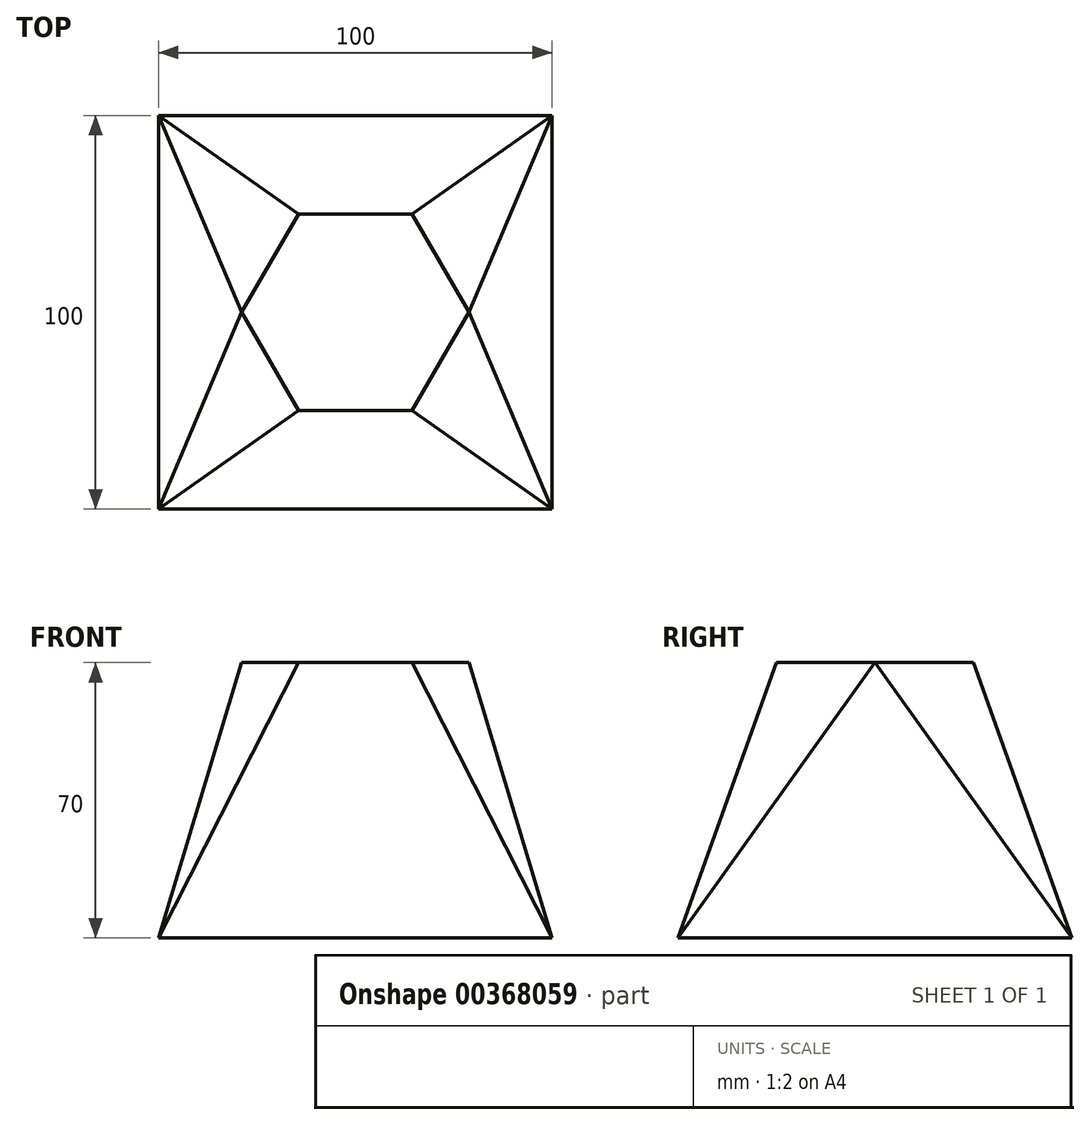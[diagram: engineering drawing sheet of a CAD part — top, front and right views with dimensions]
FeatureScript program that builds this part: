
annotation { "Feature Type Name" : "Feature", "Feature Type Description" : "" }
export const myFeature = defineFeature(function(context is Context, id is Id, definition is map)
    precondition{}
    {
        {
            var Q0;
            Q0=qCreatedBy(makeId("Top.planeOp"),FACE);
            cPlane(context, id + "F0", {"entities" : qUnion([Q0]), "cplaneType" : CPlaneType.OFFSET, "offset" : 70 * mm, "width" : 150 * mm, "height" : 150 * mm});
        }
        {
            var Q0;
            Q0=qCreatedBy(id+"F0.planeOp",FACE);
            var sketch = newSketch(context, id + "F1", { "sketchPlane" : qUnion([Q0])});
            skCircle(sketch, "E0.cCircle", {"center": v(0, 0) * mm, "radius": 25 * mm, "construction": true});
            skLineSegment(sketch, "E0.0", {"start": v(-14.43, 25) * mm, "end": v(14.43, 25) * mm});
            skLineSegment(sketch, "E0.1", {"start": v(14.43, 25) * mm, "end": v(28.87, 0) * mm});
            skLineSegment(sketch, "E0.2", {"start": v(28.87, 0) * mm, "end": v(14.43, -25) * mm});
            skLineSegment(sketch, "E0.3", {"start": v(14.43, -25) * mm, "end": v(-14.43, -25) * mm});
            skLineSegment(sketch, "E0.4", {"start": v(-14.43, -25) * mm, "end": v(-28.87, 0) * mm});
            skLineSegment(sketch, "E0.5", {"start": v(-28.87, 0) * mm, "end": v(-14.43, 25) * mm});
            skPoint(sketch, "E0.0.midPoint", {"position": v(0, 25) * mm});
            skLineSegment(sketch, "E1", {"start": v(14.43, 25) * mm, "end": v(14.43, -25) * mm});
            skLineSegment(sketch, "E2", {"start": v(-14.43, 25) * mm, "end": v(-14.43, -25) * mm});
            skSolve(sketch);
        }
        {
            var Q0;
            Q0=qCreatedBy(makeId("Top.planeOp"),FACE);
            var sketch = newSketch(context, id + "F2", { "sketchPlane" : qUnion([Q0])});
            skLineSegment(sketch, "E3.bottom", {"start": v(-50, 50) * mm, "end": v(50, 50) * mm});
            skLineSegment(sketch, "E3.top", {"start": v(-50, -50) * mm, "end": v(50, -50) * mm});
            skLineSegment(sketch, "E3.left", {"start": v(-50, 50) * mm, "end": v(-50, -50) * mm});
            skLineSegment(sketch, "E3.right", {"start": v(50, 50) * mm, "end": v(50, -50) * mm});
            skPoint(sketch, "E3.middle", {"position": v(0, 0) * mm});
            skSolve(sketch);
        }
        {
            var Q0;
            Q0=makeQuery(id+"F1.imprint","IMPRINT",FACE,{"disambiguationData":[TD([[makeQuery(id+"F1.imprint","IMPRINT",EDGE,{"derivedFrom":sQuery(id+"F1.wireOp",EDGE,"E0.0")}),-1.0]])]});
            var Q1;
            Q1=makeQuery(id+"F2.imprint","IMPRINT",FACE,{"disambiguationData":[TD([[makeQuery(id+"F2.imprint","IMPRINT",EDGE,{"derivedFrom":sQuery(id+"F2.wireOp",EDGE,"E3.bottom")}),-1.0]])]});
            loft(context, id + "F3", {"sheetProfilesArray" : [{ "sheetProfileEntities" : qUnion([Q0]) }, { "sheetProfileEntities" : qUnion([Q1]) }]});
        }
        {
            var Q1;
            Q1=makeQuery(id+"F1.imprint","IMPRINT",FACE,{"disambiguationData":[TD([[makeQuery(id+"F1.imprint","IMPRINT",EDGE,{"derivedFrom":sQuery(id+"F1.wireOp",EDGE,"E0.1")}),-1.0]])]});
            var Q2;
            Q2=makeQuery(id+"F3.opLoft","MID_CAP_VERTEX",VERTEX,{"disambiguationData":[OSD([sQuery(id+"F2.wireOp",EDGE,"E3.top"),sQuery(id+"F2.wireOp",EDGE,"E3.right")])],"capPos":1.0});
            loft(context, id + "F4", {"operationType" : NewBodyOperationType.ADD, "sheetProfilesArray" : [{ "sheetProfileEntities" : qUnion([Q1]) }, { "sheetProfileEntities" : qUnion([Q2]) }]});
        }
        {
            var Q1;
            Q1=makeQuery(id+"F1.imprint","IMPRINT",FACE,{"disambiguationData":[TD([[makeQuery(id+"F1.imprint","IMPRINT",EDGE,{"derivedFrom":sQuery(id+"F1.wireOp",EDGE,"E0.1")}),-1.0]])]});
            var Q2;
            Q2=makeQuery(id+"F3.opLoft","MID_CAP_VERTEX",VERTEX,{"disambiguationData":[OSD([sQuery(id+"F2.wireOp",EDGE,"E3.bottom"),sQuery(id+"F2.wireOp",EDGE,"E3.right")])],"capPos":1.0});
            loft(context, id + "F5", {"operationType" : NewBodyOperationType.ADD, "sheetProfilesArray" : [{ "sheetProfileEntities" : qUnion([Q1]) }, { "sheetProfileEntities" : qUnion([Q2]) }]});
        }
        {
            var Q1;
            Q1=makeQuery(id+"F4.opLoft","SWEPT_FACE",FACE,{"disambiguationData":[OSD([sQuery(id+"F1.wireOp",EDGE,"E0.0"),sQuery(id+"F1.wireOp",EDGE,"E0.1"),sQuery(id+"F1.wireOp",EDGE,"E0.2"),sQuery(id+"F1.wireOp",EDGE,"E1")])]});
            var Q2;
            Q2=makeQuery(id+"F5.opLoft","SWEPT_FACE",FACE,{"disambiguationData":[OSD([sQuery(id+"F1.wireOp",EDGE,"E0.1"),sQuery(id+"F1.wireOp",EDGE,"E0.2"),sQuery(id+"F1.wireOp",EDGE,"E0.3"),sQuery(id+"F1.wireOp",EDGE,"E1")])]});
            var Q3;
            {var subQ0=sQuery(id+"F2.wireOp",EDGE,"E3.right");var subQ1=sQuery(id+"F2.wireOp",EDGE,"E3.top");Q3=makeQuery(id+"F4.boolean.opBoolean","MERGE",VERTEX,{"derivedFrom":[makeQuery(id+"F3.opLoft","MID_CAP_VERTEX",VERTEX,{"disambiguationData":[OSD([subQ1,subQ0])],"capPos":1.0}),makeQuery(id+"F4.opLoft","SWEPT_VERTEX",VERTEX,{"disambiguationData":[OSD([sQuery(id+"F1.wireOp",EDGE,"E0.1"),sQuery(id+"F1.wireOp",EDGE,"E0.2"),subQ1,subQ0])]})]});}
            var Q4;
            {var subQ0=sQuery(id+"F2.wireOp",EDGE,"E3.right");var subQ1=sQuery(id+"F2.wireOp",EDGE,"E3.bottom");Q4=makeQuery(id+"F5.boolean.opBoolean","MERGE",VERTEX,{"derivedFrom":[makeQuery(id+"F3.opLoft","MID_CAP_VERTEX",VERTEX,{"disambiguationData":[OSD([subQ1,subQ0])],"capPos":1.0}),makeQuery(id+"F5.opLoft","SWEPT_VERTEX",VERTEX,{"disambiguationData":[OSD([sQuery(id+"F1.wireOp",EDGE,"E0.1"),sQuery(id+"F1.wireOp",EDGE,"E0.2"),subQ1,subQ0])]})]});}
            loft(context, id + "F6", {"operationType" : NewBodyOperationType.ADD, "sheetProfilesArray" : [{ "sheetProfileEntities" : qUnion([Q1]) }, { "sheetProfileEntities" : qUnion([Q2]) }], "matchConnections" : true, "connections" : [{ "connectionEntities" : qUnion([Q3, Q4]), "connectionEdgeQueries" : qUnion([]), "connectionEdgeParameters" : [] }]});
        }
        {
            var Q1;
            Q1=makeQuery(id+"F1.imprint","IMPRINT",FACE,{"disambiguationData":[TD([[makeQuery(id+"F1.imprint","IMPRINT",EDGE,{"derivedFrom":sQuery(id+"F1.wireOp",EDGE,"E0.4")}),-1.0]])]});
            var Q2;
            Q2=makeQuery(id+"F3.opLoft","MID_CAP_VERTEX",VERTEX,{"disambiguationData":[OSD([sQuery(id+"F2.wireOp",EDGE,"E3.top"),sQuery(id+"F2.wireOp",EDGE,"E3.left")])],"capPos":1.0});
            loft(context, id + "F7", {"operationType" : NewBodyOperationType.ADD, "sheetProfilesArray" : [{ "sheetProfileEntities" : qUnion([Q1]) }, { "sheetProfileEntities" : qUnion([Q2]) }]});
        }
        {
            var Q1;
            Q1=makeQuery(id+"F1.imprint","IMPRINT",FACE,{"disambiguationData":[TD([[makeQuery(id+"F1.imprint","IMPRINT",EDGE,{"derivedFrom":sQuery(id+"F1.wireOp",EDGE,"E0.4")}),-1.0]])]});
            var Q2;
            Q2=makeQuery(id+"F3.opLoft","MID_CAP_VERTEX",VERTEX,{"disambiguationData":[OSD([sQuery(id+"F2.wireOp",EDGE,"E3.bottom"),sQuery(id+"F2.wireOp",EDGE,"E3.left")])],"capPos":1.0});
            loft(context, id + "F8", {"operationType" : NewBodyOperationType.ADD, "sheetProfilesArray" : [{ "sheetProfileEntities" : qUnion([Q1]) }, { "sheetProfileEntities" : qUnion([Q2]) }]});
        }
        {
            var Q1;
            Q1=makeQuery(id+"F7.opLoft","SWEPT_FACE",FACE,{"disambiguationData":[OSD([sQuery(id+"F1.wireOp",EDGE,"E0.0"),sQuery(id+"F1.wireOp",EDGE,"E0.4"),sQuery(id+"F1.wireOp",EDGE,"E0.5"),sQuery(id+"F1.wireOp",EDGE,"E2")])]});
            var Q2;
            Q2=makeQuery(id+"F8.opLoft","SWEPT_FACE",FACE,{"disambiguationData":[OSD([sQuery(id+"F1.wireOp",EDGE,"E0.3"),sQuery(id+"F1.wireOp",EDGE,"E0.4"),sQuery(id+"F1.wireOp",EDGE,"E0.5"),sQuery(id+"F1.wireOp",EDGE,"E2")])]});
            var Q3;
            {var subQ0=sQuery(id+"F2.wireOp",EDGE,"E3.left");var subQ1=sQuery(id+"F2.wireOp",EDGE,"E3.bottom");Q3=makeQuery(id+"F8.boolean.opBoolean","MERGE",VERTEX,{"derivedFrom":[makeQuery(id+"F3.opLoft","MID_CAP_VERTEX",VERTEX,{"disambiguationData":[OSD([subQ1,subQ0])],"capPos":1.0}),makeQuery(id+"F8.opLoft","SWEPT_VERTEX",VERTEX,{"disambiguationData":[OSD([sQuery(id+"F1.wireOp",EDGE,"E0.3"),sQuery(id+"F1.wireOp",EDGE,"E0.4"),sQuery(id+"F1.wireOp",EDGE,"E2"),subQ1,subQ0])]})]});}
            var Q4;
            {var subQ0=sQuery(id+"F2.wireOp",EDGE,"E3.left");var subQ1=sQuery(id+"F2.wireOp",EDGE,"E3.top");Q4=makeQuery(id+"F7.boolean.opBoolean","MERGE",VERTEX,{"derivedFrom":[makeQuery(id+"F3.opLoft","MID_CAP_VERTEX",VERTEX,{"disambiguationData":[OSD([subQ1,subQ0])],"capPos":1.0}),makeQuery(id+"F7.opLoft","SWEPT_VERTEX",VERTEX,{"disambiguationData":[OSD([sQuery(id+"F1.wireOp",EDGE,"E0.3"),sQuery(id+"F1.wireOp",EDGE,"E0.4"),sQuery(id+"F1.wireOp",EDGE,"E2"),subQ1,subQ0])]})]});}
            loft(context, id + "F9", {"operationType" : NewBodyOperationType.ADD, "sheetProfilesArray" : [{ "sheetProfileEntities" : qUnion([Q1]) }, { "sheetProfileEntities" : qUnion([Q2]) }], "matchConnections" : true, "connections" : [{ "connectionEntities" : qUnion([Q3, Q4]), "connectionEdgeQueries" : qUnion([]), "connectionEdgeParameters" : [] }]});
        }
    });
